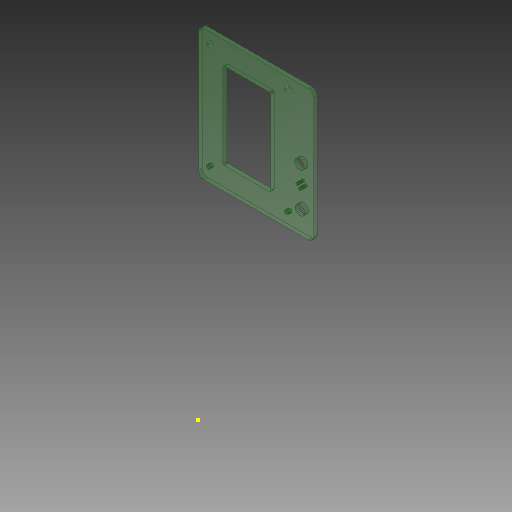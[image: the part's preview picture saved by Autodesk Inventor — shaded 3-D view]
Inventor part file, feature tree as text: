
AUTODESK INVENTOR PART (.ipt)
format: ipt  version: 2018 (Build 220112000, 112)  size: 434,688 bytes
history: native  units: mm
features: sketch x4, extrude x3, other x3, reference x1
ambient origin geometry x8: Origin, YZ Plane, XZ Plane, XY Plane, X Axis, Y Axis, Z Axis, Center Point
bodies: Solid1 (feature_tree)
feature tree (11):
  extrude  "Extrusion1"  Depth=3.0mm
  extrude  "Extrusion2"  Depth=10.0mm TaperAngle=0.0deg
  extrude  "Extrusion3"  [1 undecoded]
  sketch  "Sketch4"
  sketch  "Sketch1"  dims[d0=3.0mm d1=0.0mm d2=3.4mm]
  sketch  "Sketch2"  dims[d3=3.0mm d4=0.0mm d5=10.0mm d6=0.0mm]
  sketch  "Sketch3"
  reference  "Reference1"
  parser-record x1  (decoder bookkeeping rows leaked as tree rows — omitted from the tree; the rows remain in map.json)
  other  "LCD-Mount.iam"
  other  "Full Graphic Smart Controller:1"
note: 1 required parameter value undecoded (feature->parameter linkage not recoverable at this tier; creation-order binding heuristic only, values carry confidence <= 0.55)
note: 1 file-system path scrubbed to <path> (originals preserved in map.json)
